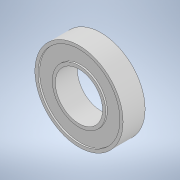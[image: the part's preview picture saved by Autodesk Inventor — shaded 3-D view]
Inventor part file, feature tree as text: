
AUTODESK INVENTOR PART (.ipt)
format: ipt  version: 2022 (Build 260153000, 153)  size: 131,072 bytes
history: native  units: mm
features: extrude x2, sketch x2, plane x1, mirror x1, projected_geometry x1
ambient origin geometry x8: Origin, YZ Plane, XZ Plane, XY Plane, X Axis, Y Axis, Z Axis, Center Point
bodies: Solid1 (feature_tree)
feature tree (7):
  extrude  "Extrusion1"  Depth=28.0mm
  extrude  "Extrusion2"  Depth=0.5mm
  plane  "Work Plane1"
  mirror  "Mirror1"
  sketch  "Sketch1"  dims[d0=15.0mm d1=28.0mm]
  sketch  "Sketch2"  dims[d2=7.0mm d3=0.0mm d4=1.0mm d5=1.0mm d6=0.5mm d7=0.0mm]
  projected_geometry  "Projected Loop1"
